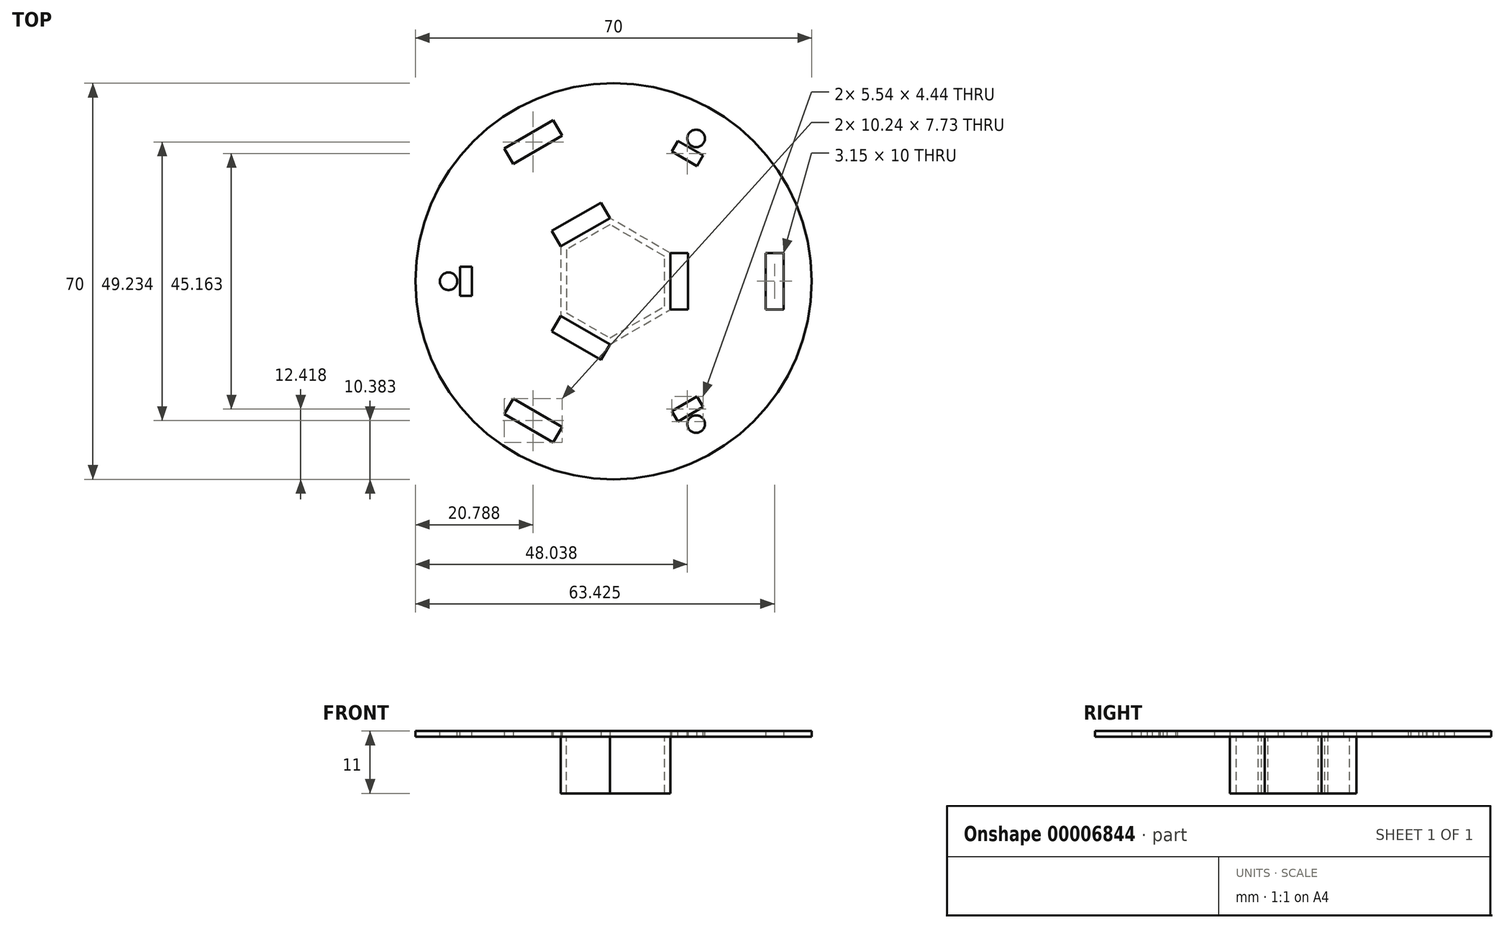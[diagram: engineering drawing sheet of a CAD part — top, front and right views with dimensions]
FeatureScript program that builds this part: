
annotation { "Feature Type Name" : "Feature", "Feature Type Description" : "" }
export const myFeature = defineFeature(function(context is Context, id is Id, definition is map)
    precondition{}
    {
        {
            var Q0;
            Q0=qCreatedBy(makeId("Top.planeOp"),FACE);
            var sketch = newSketch(context, id + "F0", { "sketchPlane" : qUnion([Q0])});
            skCircle(sketch, "E0", {"center": v(0, 0) * mm, "radius": 35 * mm});
            skLineSegment(sketch, "E1.bottom", {"start": v(30, 5) * mm, "end": v(26.85, 5) * mm});
            skLineSegment(sketch, "E1.top", {"start": v(30, -5) * mm, "end": v(26.85, -5) * mm});
            skLineSegment(sketch, "E1.left", {"start": v(30, 5) * mm, "end": v(30, -5) * mm});
            skLineSegment(sketch, "E1.right", {"start": v(26.85, 5) * mm, "end": v(26.85, -5) * mm});
            skLineSegment(sketch, "E2.bottom", {"start": v(13.15, 5) * mm, "end": v(10, 5) * mm});
            skLineSegment(sketch, "E2.top", {"start": v(13.15, -5) * mm, "end": v(10, -5) * mm});
            skLineSegment(sketch, "E2.left", {"start": v(13.15, 5) * mm, "end": v(13.15, -5) * mm});
            skLineSegment(sketch, "E2.right", {"start": v(10, 5) * mm, "end": v(10, -5) * mm});
            skPoint(sketch, "E3", {"position": v(10, 0) * mm});
            skPoint(sketch, "E4", {"position": v(26.85, 0) * mm});
            skLineSegment(sketch, "E5.1.0", {"start": v(-9.33, 6.16) * mm, "end": v(-0.67, 11.16) * mm});
            skLineSegment(sketch, "E5.1.1", {"start": v(-10.9, 8.89) * mm, "end": v(-2.24, 13.89) * mm});
            skLineSegment(sketch, "E5.1.2", {"start": v(-10.9, 8.89) * mm, "end": v(-9.33, 6.16) * mm});
            skLineSegment(sketch, "E5.1.3", {"start": v(-2.24, 13.89) * mm, "end": v(-0.67, 11.16) * mm});
            skLineSegment(sketch, "E5.1.4", {"start": v(-17.76, 20.75) * mm, "end": v(-9.1, 25.75) * mm});
            skLineSegment(sketch, "E5.1.5", {"start": v(-19.33, 23.48) * mm, "end": v(-17.76, 20.75) * mm});
            skLineSegment(sketch, "E5.1.6", {"start": v(-19.33, 23.48) * mm, "end": v(-10.67, 28.48) * mm});
            skLineSegment(sketch, "E5.1.7", {"start": v(-10.67, 28.48) * mm, "end": v(-9.1, 25.75) * mm});
            skLineSegment(sketch, "E5.2.0", {"start": v(-0.67, -11.16) * mm, "end": v(-9.33, -6.16) * mm});
            skLineSegment(sketch, "E5.2.1", {"start": v(-2.24, -13.89) * mm, "end": v(-10.9, -8.89) * mm});
            skLineSegment(sketch, "E5.2.2", {"start": v(-2.24, -13.89) * mm, "end": v(-0.67, -11.16) * mm});
            skLineSegment(sketch, "E5.2.3", {"start": v(-10.9, -8.89) * mm, "end": v(-9.33, -6.16) * mm});
            skLineSegment(sketch, "E5.2.4", {"start": v(-9.1, -25.75) * mm, "end": v(-17.76, -20.75) * mm});
            skLineSegment(sketch, "E5.2.5", {"start": v(-10.67, -28.48) * mm, "end": v(-9.1, -25.75) * mm});
            skLineSegment(sketch, "E5.2.6", {"start": v(-10.67, -28.48) * mm, "end": v(-19.33, -23.48) * mm});
            skLineSegment(sketch, "E5.2.7", {"start": v(-19.33, -23.48) * mm, "end": v(-17.76, -20.75) * mm});
            skSolve(sketch);
        }
        {
            var Q0;
            Q0=makeQuery(id+"F0.imprint","IMPRINT",FACE,{"disambiguationData":[TD([[makeQuery(id+"F0.imprint","IMPRINT",EDGE,{"derivedFrom":sQuery(id+"F0.wireOp",EDGE,"E0")}),1.0]])]});
            extrude(context, id + "F1", {"entities" : qUnion([Q0]), "depth" : 1 * mm});
        }
        {
            var Q0;
            Q0=makeQuery(id+"F1.opExtrude","CAP_FACE",FACE,{"disambiguationData":[OSD([sQuery(id+"F0.wireOp",EDGE,"E0"),sQuery(id+"F0.wireOp",EDGE,"E1.bottom"),sQuery(id+"F0.wireOp",EDGE,"E1.top"),sQuery(id+"F0.wireOp",EDGE,"E1.left"),sQuery(id+"F0.wireOp",EDGE,"E1.right"),sQuery(id+"F0.wireOp",EDGE,"E2.bottom"),sQuery(id+"F0.wireOp",EDGE,"E2.top"),sQuery(id+"F0.wireOp",EDGE,"E2.left"),sQuery(id+"F0.wireOp",EDGE,"E2.right"),sQuery(id+"F0.wireOp",EDGE,"E5.1.0"),sQuery(id+"F0.wireOp",EDGE,"E5.1.1"),sQuery(id+"F0.wireOp",EDGE,"E5.1.2"),sQuery(id+"F0.wireOp",EDGE,"E5.1.3"),sQuery(id+"F0.wireOp",EDGE,"E5.1.4"),sQuery(id+"F0.wireOp",EDGE,"E5.1.5"),sQuery(id+"F0.wireOp",EDGE,"E5.1.6"),sQuery(id+"F0.wireOp",EDGE,"E5.1.7"),sQuery(id+"F0.wireOp",EDGE,"E5.2.0"),sQuery(id+"F0.wireOp",EDGE,"E5.2.1"),sQuery(id+"F0.wireOp",EDGE,"E5.2.2"),sQuery(id+"F0.wireOp",EDGE,"E5.2.3"),sQuery(id+"F0.wireOp",EDGE,"E5.2.4"),sQuery(id+"F0.wireOp",EDGE,"E5.2.5"),sQuery(id+"F0.wireOp",EDGE,"E5.2.6"),sQuery(id+"F0.wireOp",EDGE,"E5.2.7")])],"isStart":false});
            var sketch = newSketch(context, id + "F2", { "sketchPlane" : qUnion([Q0])});
            skLineSegment(sketch, "E6", {"start": v(14.73, 20.36) * mm, "end": v(15.8, 22.23) * mm});
            skLineSegment(sketch, "E7", {"start": v(15.8, 22.23) * mm, "end": v(11.34, 24.8) * mm});
            skLineSegment(sketch, "E8", {"start": v(11.34, 24.8) * mm, "end": v(10.27, 22.94) * mm});
            skLineSegment(sketch, "E9", {"start": v(10.27, 22.94) * mm, "end": v(14.73, 20.36) * mm});
            skPoint(sketch, "E10", {"position": v(12.5, 21.65) * mm});
            skPoint(sketch, "E11", {"position": v(13.58, 23.51) * mm});
            skLineSegment(sketch, "E12", {"start": v(0, 0) * mm, "end": v(13.58, 23.51) * mm, "construction": true});
            skLineSegment(sketch, "E13.1.0", {"start": v(-27.15, -2.57) * mm, "end": v(-25, -2.57) * mm});
            skLineSegment(sketch, "E13.1.1", {"start": v(-25, 2.58) * mm, "end": v(-27.15, 2.58) * mm});
            skLineSegment(sketch, "E13.1.2", {"start": v(-27.15, 2.58) * mm, "end": v(-27.15, -2.57) * mm});
            skLineSegment(sketch, "E13.1.3", {"start": v(-25, -2.57) * mm, "end": v(-25, 2.58) * mm});
            skLineSegment(sketch, "E13.2.0", {"start": v(15.8, -22.23) * mm, "end": v(14.73, -20.36) * mm});
            skLineSegment(sketch, "E13.2.1", {"start": v(10.27, -22.94) * mm, "end": v(11.34, -24.8) * mm});
            skLineSegment(sketch, "E13.2.2", {"start": v(11.34, -24.8) * mm, "end": v(15.8, -22.23) * mm});
            skLineSegment(sketch, "E13.2.3", {"start": v(14.73, -20.36) * mm, "end": v(10.27, -22.94) * mm});
            skPoint(sketch, "E13.center", {"position": v(0, 0) * mm});
            skCircle(sketch, "E14", {"center": v(14.58, 25.24) * mm, "radius": 1.55 * mm});
            skCircle(sketch, "E15.1.0", {"center": v(-29.15, 0) * mm, "radius": 1.55 * mm});
            skCircle(sketch, "E15.2.0", {"center": v(14.57, -25.24) * mm, "radius": 1.55 * mm});
            skSolve(sketch);
        }
        {
            var Q0;
            Q0 = qSketchRegion(id + "F2", true);
            extrude(context, id + "F3", {"entities" : qUnion([Q0]), "operationType" : NewBodyOperationType.REMOVE, "endBound" : BoundingType.UP_TO_NEXT, "oppositeDirection" : true, "depth" : 25 * mm});
        }
        {
            var Q0;
            Q0=makeQuery(id+"F1.opExtrude","CAP_FACE",FACE,{"disambiguationData":[OSD([sQuery(id+"F0.wireOp",EDGE,"E0"),sQuery(id+"F0.wireOp",EDGE,"E1.bottom"),sQuery(id+"F0.wireOp",EDGE,"E1.top"),sQuery(id+"F0.wireOp",EDGE,"E1.left"),sQuery(id+"F0.wireOp",EDGE,"E1.right"),sQuery(id+"F0.wireOp",EDGE,"E2.bottom"),sQuery(id+"F0.wireOp",EDGE,"E2.top"),sQuery(id+"F0.wireOp",EDGE,"E2.left"),sQuery(id+"F0.wireOp",EDGE,"E2.right"),sQuery(id+"F0.wireOp",EDGE,"E5.1.0"),sQuery(id+"F0.wireOp",EDGE,"E5.1.1"),sQuery(id+"F0.wireOp",EDGE,"E5.1.2"),sQuery(id+"F0.wireOp",EDGE,"E5.1.3"),sQuery(id+"F0.wireOp",EDGE,"E5.1.4"),sQuery(id+"F0.wireOp",EDGE,"E5.1.5"),sQuery(id+"F0.wireOp",EDGE,"E5.1.6"),sQuery(id+"F0.wireOp",EDGE,"E5.1.7"),sQuery(id+"F0.wireOp",EDGE,"E5.2.0"),sQuery(id+"F0.wireOp",EDGE,"E5.2.1"),sQuery(id+"F0.wireOp",EDGE,"E5.2.2"),sQuery(id+"F0.wireOp",EDGE,"E5.2.3"),sQuery(id+"F0.wireOp",EDGE,"E5.2.4"),sQuery(id+"F0.wireOp",EDGE,"E5.2.5"),sQuery(id+"F0.wireOp",EDGE,"E5.2.6"),sQuery(id+"F0.wireOp",EDGE,"E5.2.7")])],"isStart":true});
            var sketch = newSketch(context, id + "F4", { "sketchPlane" : qUnion([Q0])});
            skLineSegment(sketch, "E16", {"start": v(-0.67, 11.16) * mm, "end": v(10, 5) * mm});
            skLineSegment(sketch, "E17", {"start": v(10, 5) * mm, "end": v(10, -5) * mm});
            skLineSegment(sketch, "E18", {"start": v(10, -5) * mm, "end": v(-0.67, -11.16) * mm});
            skLineSegment(sketch, "E19", {"start": v(-0.67, -11.16) * mm, "end": v(-9.33, -6.16) * mm});
            skLineSegment(sketch, "E20", {"start": v(-9.33, -6.16) * mm, "end": v(-9.33, 6.16) * mm});
            skLineSegment(sketch, "E21", {"start": v(-9.33, 6.16) * mm, "end": v(-0.67, 11.16) * mm});
            skLineSegment(sketch, "E22.0", {"start": v(-8.33, 5.58) * mm, "end": v(-0.67, 10) * mm});
            skLineSegment(sketch, "E22.1", {"start": v(-8.33, -5.58) * mm, "end": v(-8.33, 5.58) * mm});
            skLineSegment(sketch, "E22.2", {"start": v(-0.67, -10) * mm, "end": v(-8.33, -5.58) * mm});
            skLineSegment(sketch, "E22.3", {"start": v(9, -4.42) * mm, "end": v(-0.67, -10) * mm});
            skLineSegment(sketch, "E22.4", {"start": v(9, 4.42) * mm, "end": v(9, -4.42) * mm});
            skLineSegment(sketch, "E22.5", {"start": v(-0.67, 10) * mm, "end": v(9, 4.42) * mm});
            skSolve(sketch);
        }
        {
            var Q0;
            Q0=makeQuery(id+"F4.imprint","IMPRINT",FACE,{"disambiguationData":[TD([[makeQuery(id+"F4.imprint","IMPRINT",EDGE,{"derivedFrom":sQuery(id+"F4.wireOp",EDGE,"E16")}),-1.0]])]});
            extrude(context, id + "F5", {"entities" : qUnion([Q0]), "operationType" : NewBodyOperationType.ADD, "depth" : 10 * mm});
        }
    });
